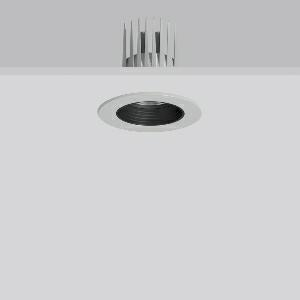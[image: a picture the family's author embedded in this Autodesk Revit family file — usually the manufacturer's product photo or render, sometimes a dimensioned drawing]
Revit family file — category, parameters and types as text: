
# Revit family: heledon_mini_e_901752_004_3_e3b6
name_source: partatom
category: Lighting Fixtures
units: mm (PartAtom-declared; Revit-internal decimal feet)

## family parameters
Cut with Voids When Loaded = No
Host = Face
Light Source = No
Part Type = Normal
Room Calculation Point = No
Round Connector Dimension = Use Diameter
Shared = No

## types (1)
- HELEDON mini E (1 x LED Modul 935, 3050 lm, 3500)
    Apparent Load = 29 VA
    Approval mark = CE
    CIE Flux Codes = 96 100 100 100 100
    Color Rendering = 92
    Color Temperature = 3500
    Default Elevation = 1800 mm
    Description = Series: HELEDON mini
Round recessed downlight. Housing: die-cast aluminium, powder-coated. Black plastic ring and recessed LED to prevent glare from the side. Optical assembly with lens made of plastic (polycarbonate) for the best homogeneous light distribution - can be changed without tools. Best colour rendering index Ra>90. Suitable for Recessed ceiling mounting. Installation without tools thanks to spring fastening system. Including separate LED converter with connecting cable 600 mm.High quality converter without flickering and stroboscopic effect. Through-wiring box (5 pole) available as accessory. The following accessories can be mounted without use of tools: interchangeable lenses, decorative glasses, honeycomb louvre, clear and frosted diffusers, white interchangeable plastic ring. 
Colour: silver
Diameter: 124 mm
Height: 3 mm
Cut-out diameter: 114 mm
Recess height: 170 mm
Luminaire: recess height: 120 mm
Lamp: LED
Socket: without socket
Colour temperature: 3500K
Colour rendering index (CRI): 92
System power: 29 W
Rated luminous flux: 3050 lm
Luminous efficiency: 105 lm/W
Control gear: Regulated power supply
Protection class: II
Type of protection: IP 20
    Height = 0 mm  [stored 0 ft]
    Lamp = 1 x LED Modul 935
    Lamp Light Flux = 3050 lm
    Lamp count = 1
    Length = 124 mm  [stored 0.406824 ft]
    Lifetime = 50000 h
    Luminous efficacy = 105 lm/W
    Manufacturer = RZB
    ModVariant = No
    Model = 901752.004.3
    Mounting Place = Ceiling
    Mounting Type = Recessed
    Number of Poles = 1
    OnlyDefault = Yes
    Power Factor = 1
    Product Name = HELEDON mini E
    Product group = Recessed downlights
    ProductGroupID = 402
    Protection Class = Protection class II
    Protection Degree = IP 20
    RLX_Detail_Level = 1
    RLX_Emergency_Light_Flux = 0 lm
    RLX_Emergency_Type = 0
    RLX_Emergency_Type_DB = No
    RlxData = <blob elided: 127789 chars, md5=de3e0b07>
    Socket = socket
    Standby Power = 0 W
    System Light Flux = 3050 lm
    System Power = 29 W
    Type Comments = Product without accessories
    Type Image = 901656.004.jpg
    URL = http://relux.com
    VarID = ---
    Voltage = 230 V
    Voltage Range = 220-240 V
    Weight = 0.00 kg
    Width = 0 mm  [stored 0 ft]

note: [stored X ft] marks values corroborated as IEEE doubles in the binary element streams (Revit-internal decimal feet)

## geometry (parser evidence)
native form markers: Blend x4, Sweep x11
no freeform markers — native parametric forms only
